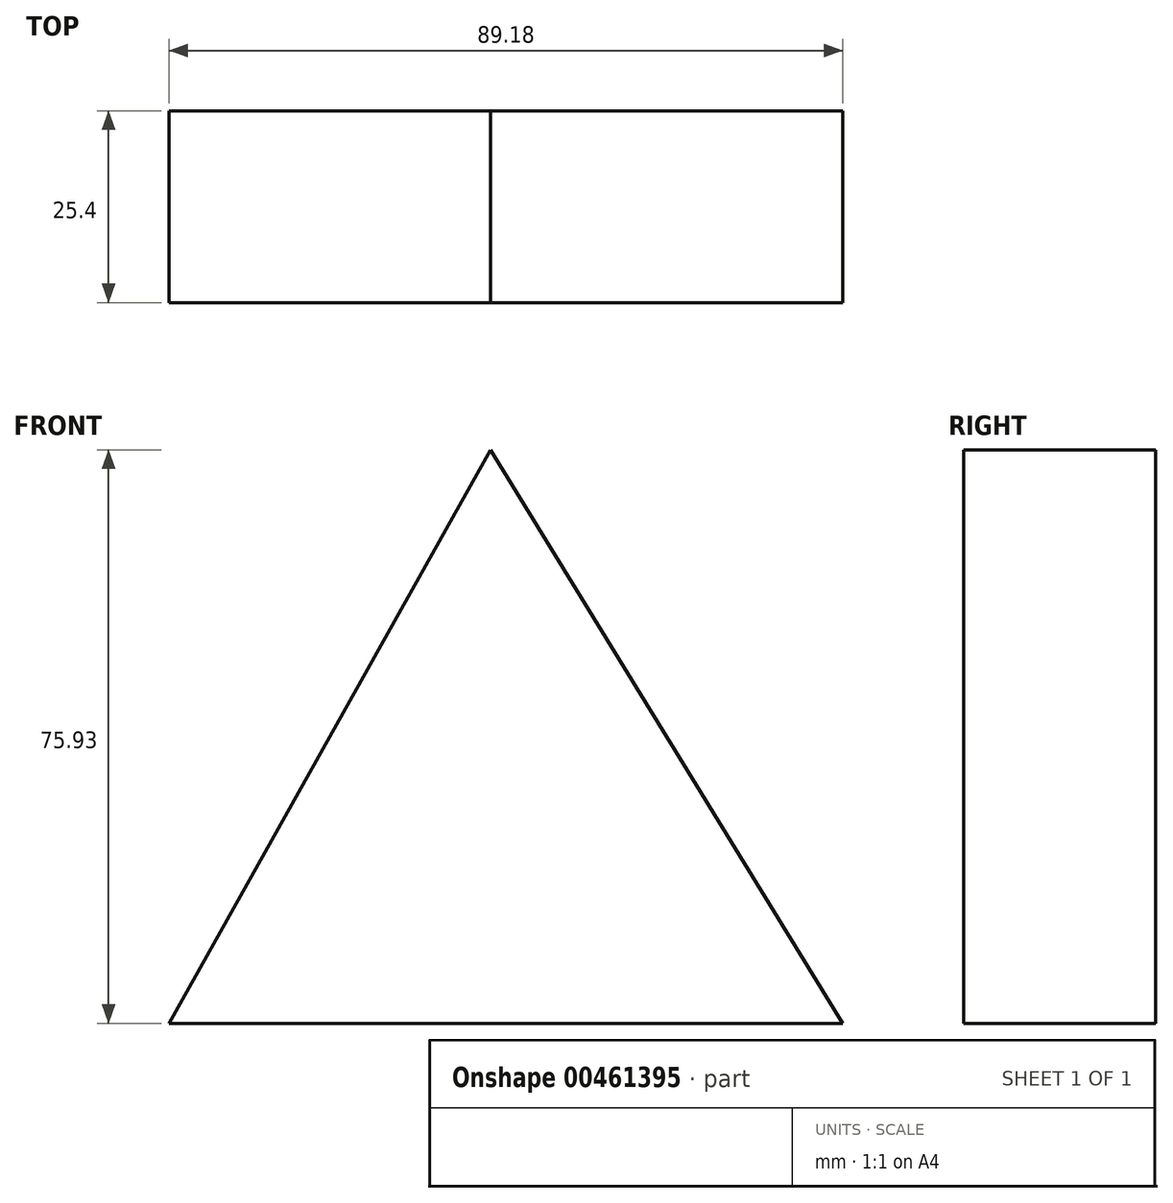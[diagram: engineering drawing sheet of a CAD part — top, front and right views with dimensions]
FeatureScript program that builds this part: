
annotation { "Feature Type Name" : "Feature", "Feature Type Description" : "" }
export const myFeature = defineFeature(function(context is Context, id is Id, definition is map)
    precondition{}
    {
        {
            var Q0;
            Q0=qCreatedBy(makeId("Front.planeOp"),FACE);
            var sketch = newSketch(context, id + "F0", { "sketchPlane" : qUnion([Q0])});
            skLineSegment(sketch, "E0", {"start": v(-42.55, 0) * mm, "end": v(46.63, 0) * mm});
            skLineSegment(sketch, "E1", {"start": v(46.63, 0) * mm, "end": v(0, 75.93) * mm});
            skLineSegment(sketch, "E2", {"start": v(0, 75.93) * mm, "end": v(-42.55, 0) * mm});
            skSolve(sketch);
        }
        {
            var Q0;
            Q0=makeQuery(id+"F0.imprint","IMPRINT",FACE,{"disambiguationData":[TD([[makeQuery(id+"F0.imprint","IMPRINT",EDGE,{"derivedFrom":sQuery(id+"F0.wireOp",EDGE,"E0")}),1.0]])]});
            extrude(context, id + "F1", {"entities" : qUnion([Q0]), "depth" : 25.4 * mm});
        }
    });
